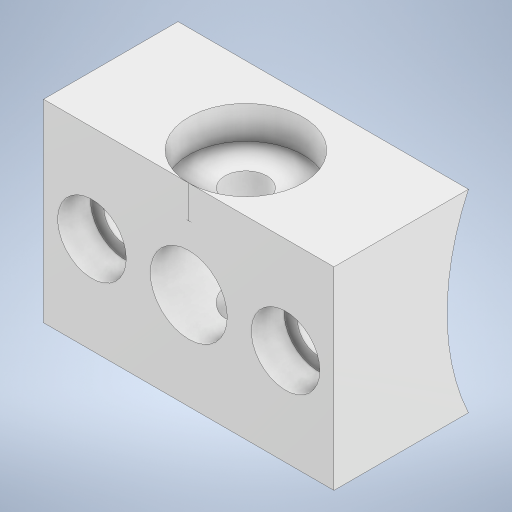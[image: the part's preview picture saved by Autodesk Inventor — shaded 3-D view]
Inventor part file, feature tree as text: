
AUTODESK INVENTOR PART (.ipt)
format: ipt  version: 2023 (Build 270158030, 158C)  size: 265,216 bytes
history: native  units: in
note: dims shown in document units (in); Inventor stores cm internally (conversion verified against a paired STEP export)
features: sketch x4, extrude x2, hole x2
ambient origin geometry x8: Origin, YZ Plane, XZ Plane, XY Plane, X Axis, Y Axis, Z Axis, Center Point
bodies: Solid1 (feature_tree)
feature tree (8):
  extrude  "Extrusion1"  Depth=1.5in TaperAngle=0.0deg
  extrude  "Extrusion6"  Depth=1.0in
  hole  "Hole2"  [1 undecoded]
  hole  "Hole3"  [1 undecoded]
  sketch  "Sketch1"  dims[d0=2.375in d4=1.5in d5=0.0in]
  sketch  "Sketch8"  dims[d47=1.7717in d48=1.0in]
  sketch  "Sketch10"  dims[d49=0.3976in d50=0.0in d51=0.0in]
  sketch  "Sketch11"  dims[d52=0.2165in d53=0.2362in d54=0.5906in d55=0.1693in d56=0.5635in d57=0.315in d58=0.8108in d60=0.2953in d61=0.2165in d62=0.2362in d63=0.3543in d64=0.1693in d65=90.0deg d66=0.315in d67=0.8108in d68=1.0in d69=0.0394in d70=0.0394in d71=0.0394in d72=0.0059in d73=0.2165in d74=0.0148in d75=0.5635in d76=0.0295in d77=0.8108in d78=0.0025in d79=0.0295in d80=0.0148in]
note: 2 required parameter values undecoded (feature->parameter linkage not recoverable at this tier; creation-order binding heuristic only, values carry confidence <= 0.55)
